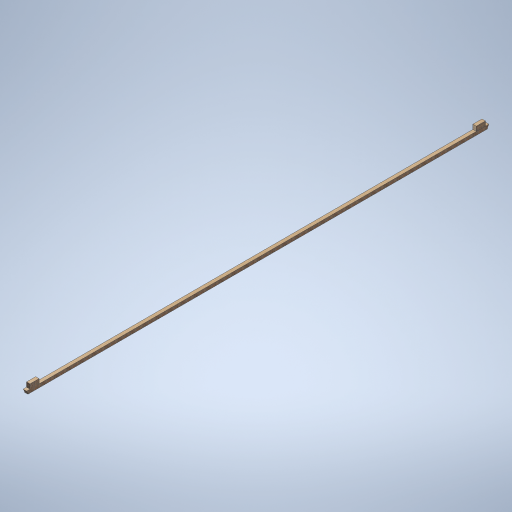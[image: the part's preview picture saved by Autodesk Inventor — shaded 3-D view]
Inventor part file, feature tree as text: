
AUTODESK INVENTOR PART (.ipt)
format: ipt  version: 2024.2 (Build 282272000, 272)  size: 330,752 bytes
history: native  units: mm
features: sketch x8, extrude x4
ambient origin geometry x8: Origin, YZ Plane, XZ Plane, XY Plane, X Axis, Y Axis, Z Axis, Center Point
bodies: Solid1 (feature_tree)
feature tree (12):
  sketch  "Sketch1"  dims[d0=300.0mm d1=300.0mm]
  extrude  "Extrusion1"  Depth=300.0mm
  sketch  "Sketch4"  dims[d11=250.0mm d12=60.0deg]
  sketch  "Sketch5"  dims[d13=25.307274mm d14=300.0mm d15=0.0mm]
  extrude  "Extrusion3"  Depth=1000.0mm
  sketch  "Sketch7"  dims[d17=799.0mm]
  extrude  "Extrusion4"  TaperAngle=60.0deg  [1 undecoded]
  extrude  "Extrusion5"  Depth=300.0mm TaperAngle=0.0deg
  sketch  "Sketch2"  dims[d2=38608.0mm d3=0.0mm d10=1000.0mm]
  sketch  "Sketch6"  dims[d16=304.0mm]
  sketch  "Sketch8"  dims[d18=304.0mm]
  sketch  "Sketch9"  dims[d19=799.0mm d20=90.0deg d21=400.0mm d22=0.0mm d23=300.0mm d24=0.0mm d4=500.0mm d5=0.872665mm]
note: 1 required parameter value undecoded (feature->parameter linkage not recoverable at this tier; creation-order binding heuristic only, values carry confidence <= 0.55)
